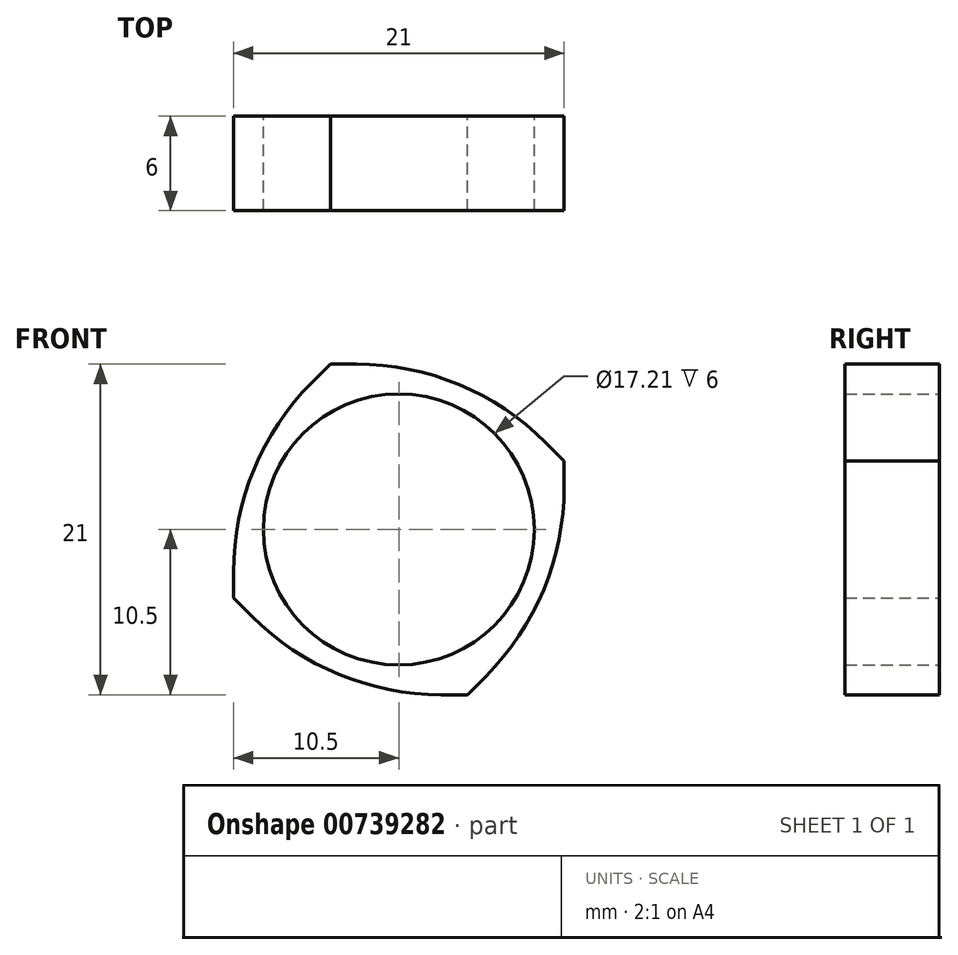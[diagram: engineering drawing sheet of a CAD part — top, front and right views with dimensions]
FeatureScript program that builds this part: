
annotation { "Feature Type Name" : "Feature", "Feature Type Description" : "" }
export const myFeature = defineFeature(function(context is Context, id is Id, definition is map)
    precondition{}
    {
        {
            var Q0;
            Q0=qCreatedBy(makeId("Front.planeOp"),FACE);
            var sketch = newSketch(context, id + "F0", { "sketchPlane" : qUnion([Q0])});
            skCircle(sketch, "E0", {"center": v(0, 0) * mm, "radius": 8.6 * mm});
            skCircle(sketch, "E1.cCircle", {"center": v(0, 0) * mm, "radius": 10.5 * mm, "construction": true});
            skLineSegment(sketch, "E1.0", {"start": v(4.35, -10.5) * mm, "end": v(-4.35, -10.5) * mm});
            skLineSegment(sketch, "E1.1", {"start": v(-4.35, -10.5) * mm, "end": v(-10.5, -4.35) * mm});
            skLineSegment(sketch, "E1.2", {"start": v(-10.5, -4.35) * mm, "end": v(-10.5, 4.35) * mm});
            skLineSegment(sketch, "E1.3", {"start": v(-10.5, 4.35) * mm, "end": v(-4.35, 10.5) * mm});
            skLineSegment(sketch, "E1.4", {"start": v(-4.35, 10.5) * mm, "end": v(4.35, 10.5) * mm});
            skLineSegment(sketch, "E1.5", {"start": v(4.35, 10.5) * mm, "end": v(10.5, 4.35) * mm});
            skLineSegment(sketch, "E1.6", {"start": v(10.5, 4.35) * mm, "end": v(10.5, -4.35) * mm});
            skLineSegment(sketch, "E1.7", {"start": v(10.5, -4.35) * mm, "end": v(4.35, -10.5) * mm});
            skPoint(sketch, "E1.0.midPoint", {"position": v(0, -10.5) * mm});
            skSolve(sketch);
        }
        {
            var Q0;
            Q0 = qSketchRegion(id + "F0", true);
            extrude(context, id + "F1", {"entities" : qUnion([Q0]), "depth" : 6 * mm, "offsetDistance" : 25 * mm});
        }
        {
            var Q0;
            Q0=makeQuery(id+"F1.opExtrude","SWEPT_EDGE",EDGE,{"disambiguationData":[OSD([sQuery(id+"F0.wireOp",EDGE,"E1.2"),sQuery(id+"F0.wireOp",EDGE,"E1.3")])]});
            var Q1;
            Q1=makeQuery(id+"F1.opExtrude","SWEPT_EDGE",EDGE,{"disambiguationData":[OSD([sQuery(id+"F0.wireOp",EDGE,"E1.4"),sQuery(id+"F0.wireOp",EDGE,"E1.5")])]});
            var Q2;
            Q2=makeQuery(id+"F1.opExtrude","SWEPT_EDGE",EDGE,{"disambiguationData":[OSD([sQuery(id+"F0.wireOp",EDGE,"E1.6"),sQuery(id+"F0.wireOp",EDGE,"E1.7")])]});
            var Q3;
            Q3=makeQuery(id+"F1.opExtrude","SWEPT_EDGE",EDGE,{"disambiguationData":[OSD([sQuery(id+"F0.wireOp",EDGE,"E1.0"),sQuery(id+"F0.wireOp",EDGE,"E1.1")])]});
            fillet(context, id + "F2", {"entities" : qUnion([Q0, Q1, Q2, Q3]), "radius" : 17 * mm, "tangentPropagation" : true, "allowEdgeOverflow" : false});
        }
    });
